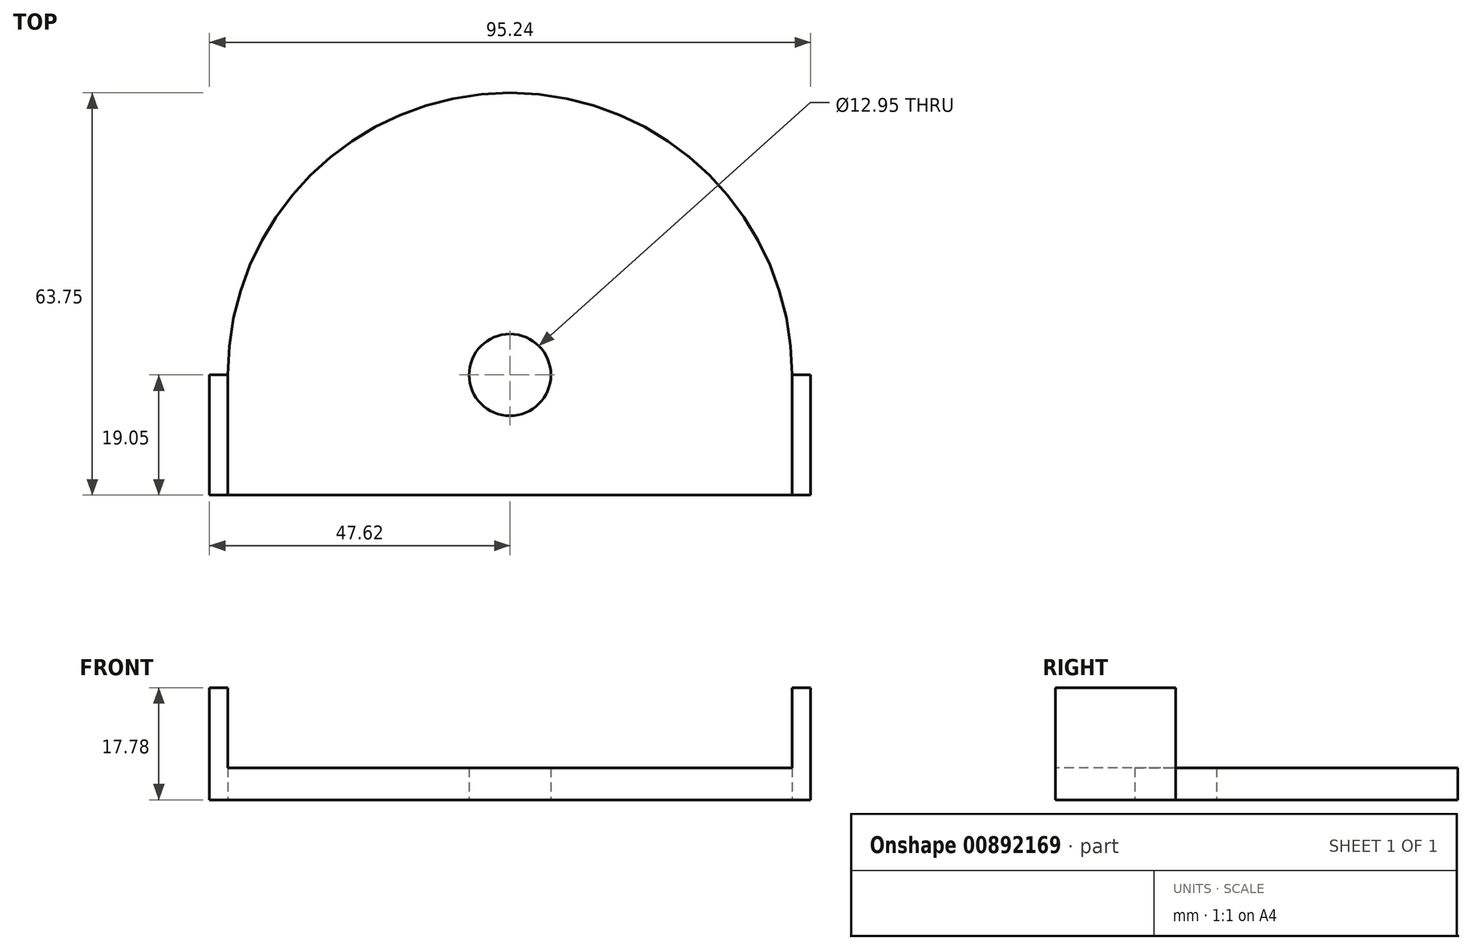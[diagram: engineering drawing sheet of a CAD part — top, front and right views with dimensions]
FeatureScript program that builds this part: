
annotation { "Feature Type Name" : "Feature", "Feature Type Description" : "" }
export const myFeature = defineFeature(function(context is Context, id is Id, definition is map)
    precondition{}
    {
        {
            var Q0;
            Q0=qCreatedBy(makeId("Top.planeOp"),FACE);
            var sketch = newSketch(context, id + "F0", { "sketchPlane" : qUnion([Q0])});
            skArc(sketch, "E0", {"start": v(44.7, 0) * mm, "mid": v(0, 44.7) * mm, "end": v(-44.7, 0) * mm});
            skLineSegment(sketch, "E1.bottom", {"start": v(-47.63, 0) * mm, "end": v(-44.7, 0) * mm});
            skLineSegment(sketch, "E1.top", {"start": v(-47.63, -19.05) * mm, "end": v(47.63, -19.05) * mm});
            skLineSegment(sketch, "E1.left", {"start": v(-47.63, 0) * mm, "end": v(-47.63, -19.05) * mm});
            skLineSegment(sketch, "E1.right", {"start": v(47.63, 0) * mm, "end": v(47.63, -19.05) * mm});
            skLineSegment(sketch, "E2.trimOffspring", {"start": v(44.7, 0) * mm, "end": v(47.63, 0) * mm});
            skCircle(sketch, "E3", {"center": v(0, 0) * mm, "radius": 6.48 * mm});
            skSolve(sketch);
        }
        {
            var Q0;
            Q0 = qSketchRegion(id + "F0", true);
            extrude(context, id + "F1", {"entities" : qUnion([Q0]), "depth" : 5.08 * mm, "offsetDistance" : 25.4 * mm});
        }
        {
            var Q0;
            Q0=makeQuery(id+"F1.opExtrude","CAP_FACE",FACE,{"disambiguationData":[OSD([sQuery(id+"F0.wireOp",EDGE,"E0"),sQuery(id+"F0.wireOp",EDGE,"E1.bottom"),sQuery(id+"F0.wireOp",EDGE,"E1.top"),sQuery(id+"F0.wireOp",EDGE,"E1.left"),sQuery(id+"F0.wireOp",EDGE,"E1.right"),sQuery(id+"F0.wireOp",EDGE,"E2.trimOffspring"),sQuery(id+"F0.wireOp",EDGE,"E3")])],"isStart":false});
            var sketch = newSketch(context, id + "F2", { "sketchPlane" : qUnion([Q0])});
            skLineSegment(sketch, "E4.bottom", {"start": v(-44.7, 0) * mm, "end": v(-47.63, 0) * mm});
            skLineSegment(sketch, "E4.top", {"start": v(-44.7, -19.05) * mm, "end": v(-47.63, -19.05) * mm});
            skLineSegment(sketch, "E4.left", {"start": v(-44.7, 0) * mm, "end": v(-44.7, -19.05) * mm});
            skLineSegment(sketch, "E4.right", {"start": v(-47.63, 0) * mm, "end": v(-47.63, -19.05) * mm});
            skLineSegment(sketch, "E5.bottom", {"start": v(44.7, 0) * mm, "end": v(47.63, 0) * mm});
            skLineSegment(sketch, "E5.top", {"start": v(44.7, -19.05) * mm, "end": v(47.63, -19.05) * mm});
            skLineSegment(sketch, "E5.left", {"start": v(44.7, 0) * mm, "end": v(44.7, -19.05) * mm});
            skLineSegment(sketch, "E5.right", {"start": v(47.63, 0) * mm, "end": v(47.63, -19.05) * mm});
            skSolve(sketch);
        }
        {
            var Q0;
            Q0 = qSketchRegion(id + "F2", true);
            extrude(context, id + "F3", {"entities" : qUnion([Q0]), "operationType" : NewBodyOperationType.ADD, "depth" : 12.7 * mm, "offsetDistance" : 25.4 * mm});
        }
    });
